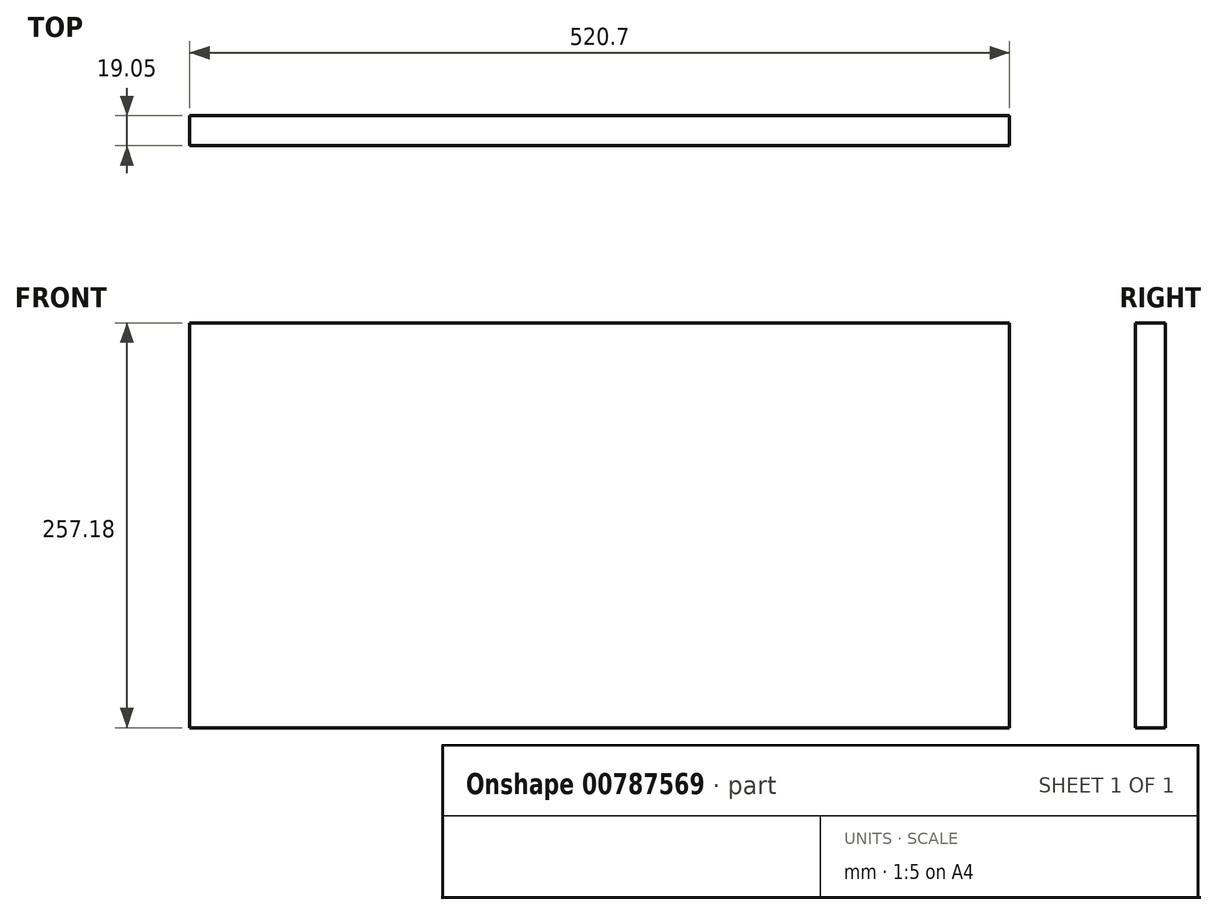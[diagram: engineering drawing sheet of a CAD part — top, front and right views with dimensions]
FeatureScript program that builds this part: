
annotation { "Feature Type Name" : "Feature", "Feature Type Description" : "" }
export const myFeature = defineFeature(function(context is Context, id is Id, definition is map)
    precondition{}
    {
        {
            var Q0;
            Q0=qCreatedBy(makeId("Front.planeOp"),FACE);
            var sketch = newSketch(context, id + "F0", { "sketchPlane" : qUnion([Q0])});
            skLineSegment(sketch, "E0.bottom", {"start": v(260.35, 128.59) * mm, "end": v(-260.35, 128.59) * mm});
            skLineSegment(sketch, "E0.top", {"start": v(260.35, -128.59) * mm, "end": v(-260.35, -128.59) * mm});
            skLineSegment(sketch, "E0.left", {"start": v(260.35, 128.59) * mm, "end": v(260.35, -128.59) * mm});
            skLineSegment(sketch, "E0.right", {"start": v(-260.35, 128.59) * mm, "end": v(-260.35, -128.59) * mm});
            skPoint(sketch, "E0.middle", {"position": v(0, 0) * mm});
            skSolve(sketch);
        }
        {
            var Q0;
            Q0=makeQuery(id+"F0.imprint","IMPRINT",FACE,{"disambiguationData":[TD([[makeQuery(id+"F0.imprint","IMPRINT",EDGE,{"derivedFrom":sQuery(id+"F0.wireOp",EDGE,"E0.bottom")}),1.0]])]});
            extrude(context, id + "F1", {"entities" : qUnion([Q0]), "depth" : 19.05 * mm, "offsetDistance" : 25.4 * mm});
        }
    });
